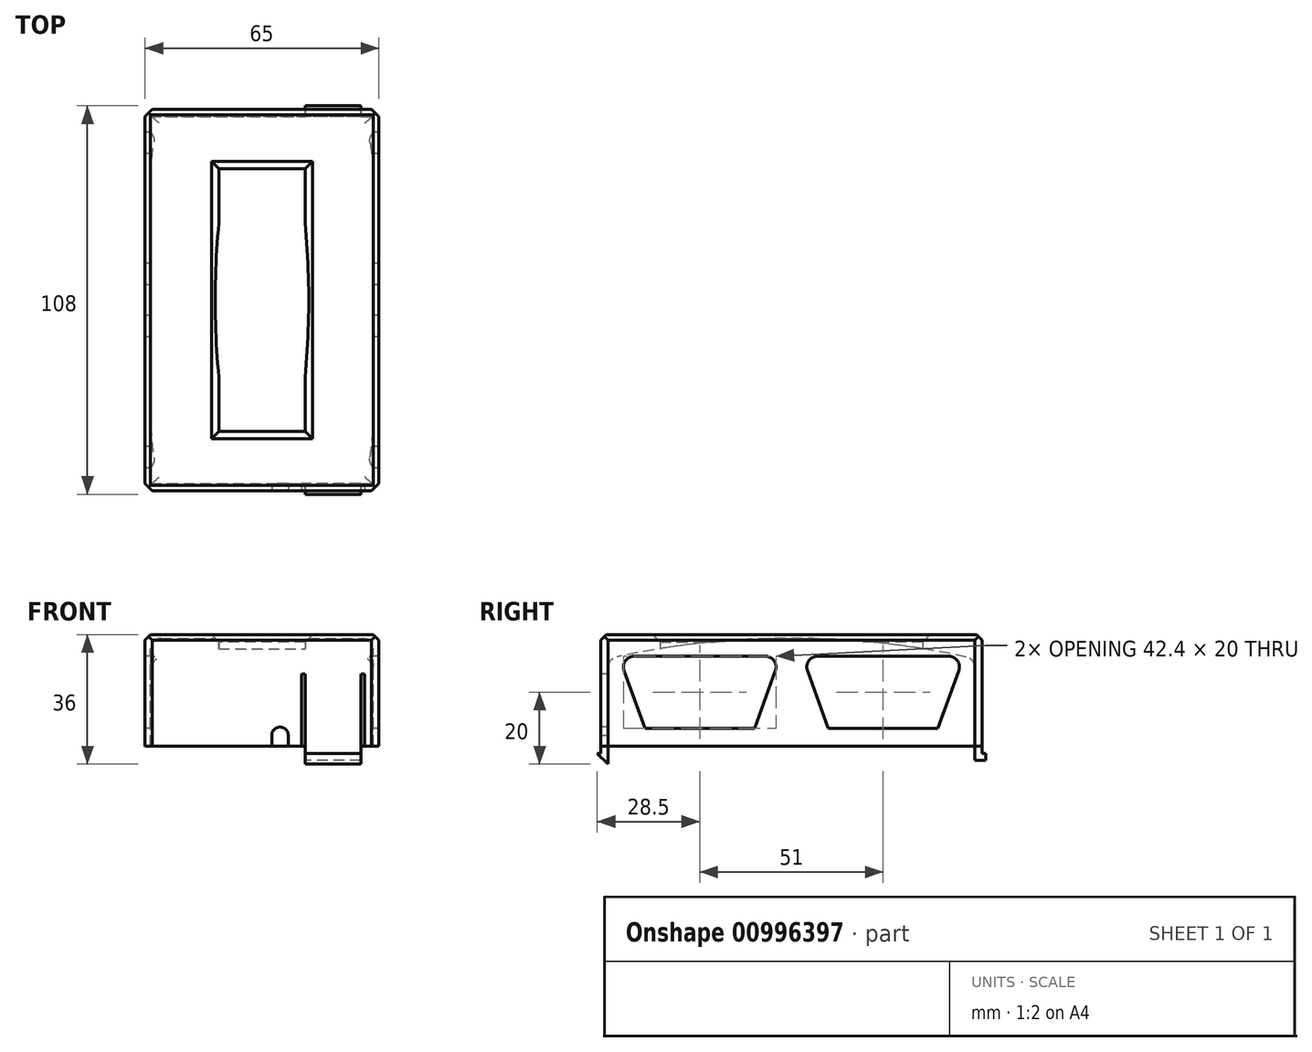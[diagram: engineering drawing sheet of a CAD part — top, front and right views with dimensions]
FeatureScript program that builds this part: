
annotation { "Feature Type Name" : "Feature", "Feature Type Description" : "" }
export const myFeature = defineFeature(function(context is Context, id is Id, definition is map)
    precondition{}
    {
        {
            var Q0;
            Q0=qCreatedBy(makeId("Top.planeOp"),FACE);
            var sketch = newSketch(context, id + "F0", { "sketchPlane" : qUnion([Q0])});
            skLineSegment(sketch, "E0.bottom", {"start": v(-32.5, 53) * mm, "end": v(32.5, 53) * mm});
            skLineSegment(sketch, "E0.top", {"start": v(-32.5, -53) * mm, "end": v(32.5, -53) * mm});
            skLineSegment(sketch, "E0.left", {"start": v(-32.5, 53) * mm, "end": v(-32.5, -53) * mm});
            skLineSegment(sketch, "E0.right", {"start": v(32.5, 53) * mm, "end": v(32.5, -53) * mm});
            skSolve(sketch);
        }
        {
            var Q0;
            Q0 = qSketchRegion(id + "F0", true);
            extrude(context, id + "F1", {"entities" : qUnion([Q0]), "depth" : 31 * mm, "offsetDistance" : 25 * mm});
        }
        {
            var Q0;
            Q0=qCreatedBy(makeId("Right.planeOp"),FACE);
            var sketch = newSketch(context, id + "F2", { "sketchPlane" : qUnion([Q0])});
            skLineSegment(sketch, "E1.bottom", {"start": v(-51, 0) * mm, "end": v(51, 0) * mm});
            skLineSegment(sketch, "E1.left", {"start": v(-51, 0) * mm, "end": v(-51, 24.27) * mm});
            skLineSegment(sketch, "E1.right", {"start": v(51, 0) * mm, "end": v(51, 24.27) * mm});
            skArc(sketch, "E2", {"start": v(51, 24.27) * mm, "mid": v(0, 30) * mm, "end": v(-51, 24.27) * mm});
            skSolve(sketch);
        }
        {
            var Q0;
            Q0 = qSketchRegion(id + "F2", true);
            extrude(context, id + "F3", {"entities" : qUnion([Q0]), "operationType" : NewBodyOperationType.REMOVE, "endBound" : BoundingType.SYMMETRIC, "oppositeDirection" : true, "depth" : 62 * mm, "offsetDistance" : 25 * mm});
        }
        {
            var Q0;
            Q0=qCreatedBy(makeId("Top.planeOp"),FACE);
            var sketch = newSketch(context, id + "F4", { "sketchPlane" : qUnion([Q0])});
            skLineSegment(sketch, "E3.bottom", {"start": v(-12, 36.5) * mm, "end": v(12, 36.5) * mm});
            skLineSegment(sketch, "E3.top", {"start": v(-12, -36.5) * mm, "end": v(12, -36.5) * mm});
            skLineSegment(sketch, "E3.left", {"start": v(-12, 36.5) * mm, "end": v(-12, -36.5) * mm});
            skLineSegment(sketch, "E3.right", {"start": v(12, 36.5) * mm, "end": v(12, -36.5) * mm});
            skSolve(sketch);
        }
        {
            var Q0;
            Q0 = qSketchRegion(id + "F4", true);
            extrude(context, id + "F5", {"entities" : qUnion([Q0]), "operationType" : NewBodyOperationType.REMOVE, "depth" : 58 * mm, "offsetDistance" : 25 * mm});
        }
        {
            var Q0;
            Q0=makeQuery(id+"F1.opExtrude","CAP_EDGE",EDGE,{"disambiguationData":[OSD([sQuery(id+"F0.wireOp",EDGE,"E0.bottom")])],"isStart":false});
            var Q1;
            Q1=makeQuery(id+"F1.opExtrude","CAP_EDGE",EDGE,{"disambiguationData":[OSD([sQuery(id+"F0.wireOp",EDGE,"E0.left")])],"isStart":false});
            var Q2;
            Q2=makeQuery(id+"F1.opExtrude","CAP_EDGE",EDGE,{"disambiguationData":[OSD([sQuery(id+"F0.wireOp",EDGE,"E0.right")])],"isStart":false});
            var Q3;
            Q3=makeQuery(id+"F1.opExtrude","CAP_EDGE",EDGE,{"disambiguationData":[OSD([sQuery(id+"F0.wireOp",EDGE,"E0.top")])],"isStart":false});
            chamfer(context, id + "F6", {"entities" : qUnion([Q0, Q1, Q2, Q3]), "width" : 1.5 * mm, "tangentPropagation" : true});
        }
        {
            var Q0;
            Q0=makeQuery(id+"F5.boolean.opBoolean","INTERSECT",EDGE,{"derivedFrom":[makeQuery(id+"F1.opExtrude","CAP_FACE",FACE,{"disambiguationData":[OSD([sQuery(id+"F0.wireOp",EDGE,"E0.bottom"),sQuery(id+"F0.wireOp",EDGE,"E0.top"),sQuery(id+"F0.wireOp",EDGE,"E0.left"),sQuery(id+"F0.wireOp",EDGE,"E0.right")])],"isStart":false}),makeQuery(id+"F5.opExtrude","SWEPT_FACE",FACE,{"disambiguationData":[OSD([sQuery(id+"F4.wireOp",EDGE,"E3.bottom")])]})]});
            var Q1;
            Q1=makeQuery(id+"F5.boolean.opBoolean","INTERSECT",EDGE,{"derivedFrom":[makeQuery(id+"F1.opExtrude","CAP_FACE",FACE,{"disambiguationData":[OSD([sQuery(id+"F0.wireOp",EDGE,"E0.bottom"),sQuery(id+"F0.wireOp",EDGE,"E0.top"),sQuery(id+"F0.wireOp",EDGE,"E0.left"),sQuery(id+"F0.wireOp",EDGE,"E0.right")])],"isStart":false}),makeQuery(id+"F5.opExtrude","SWEPT_FACE",FACE,{"disambiguationData":[OSD([sQuery(id+"F4.wireOp",EDGE,"E3.right")])]})]});
            var Q2;
            Q2=makeQuery(id+"F5.boolean.opBoolean","INTERSECT",EDGE,{"derivedFrom":[makeQuery(id+"F1.opExtrude","CAP_FACE",FACE,{"disambiguationData":[OSD([sQuery(id+"F0.wireOp",EDGE,"E0.bottom"),sQuery(id+"F0.wireOp",EDGE,"E0.top"),sQuery(id+"F0.wireOp",EDGE,"E0.left"),sQuery(id+"F0.wireOp",EDGE,"E0.right")])],"isStart":false}),makeQuery(id+"F5.opExtrude","SWEPT_FACE",FACE,{"disambiguationData":[OSD([sQuery(id+"F4.wireOp",EDGE,"E3.left")])]})]});
            var Q3;
            Q3=makeQuery(id+"F5.boolean.opBoolean","INTERSECT",EDGE,{"derivedFrom":[makeQuery(id+"F1.opExtrude","CAP_FACE",FACE,{"disambiguationData":[OSD([sQuery(id+"F0.wireOp",EDGE,"E0.bottom"),sQuery(id+"F0.wireOp",EDGE,"E0.top"),sQuery(id+"F0.wireOp",EDGE,"E0.left"),sQuery(id+"F0.wireOp",EDGE,"E0.right")])],"isStart":false}),makeQuery(id+"F5.opExtrude","SWEPT_FACE",FACE,{"disambiguationData":[OSD([sQuery(id+"F4.wireOp",EDGE,"E3.top")])]})]});
            chamfer(context, id + "F7", {"entities" : qUnion([Q0, Q1, Q2, Q3]), "width" : 2 * mm, "tangentPropagation" : true});
        }
        {
            var Q0;
            Q0=makeQuery(id+"F1.opExtrude","SWEPT_EDGE",EDGE,{"disambiguationData":[OSD([sQuery(id+"F0.wireOp",EDGE,"E0.bottom"),sQuery(id+"F0.wireOp",EDGE,"E0.left")])]});
            var Q1;
            Q1=makeQuery(id+"F1.opExtrude","SWEPT_EDGE",EDGE,{"disambiguationData":[OSD([sQuery(id+"F0.wireOp",EDGE,"E0.top"),sQuery(id+"F0.wireOp",EDGE,"E0.left")])]});
            var Q2;
            Q2=makeQuery(id+"F1.opExtrude","SWEPT_EDGE",EDGE,{"disambiguationData":[OSD([sQuery(id+"F0.wireOp",EDGE,"E0.top"),sQuery(id+"F0.wireOp",EDGE,"E0.right")])]});
            var Q3;
            Q3=makeQuery(id+"F1.opExtrude","SWEPT_EDGE",EDGE,{"disambiguationData":[OSD([sQuery(id+"F0.wireOp",EDGE,"E0.bottom"),sQuery(id+"F0.wireOp",EDGE,"E0.right")])]});
            chamfer(context, id + "F8", {"entities" : qUnion([Q0, Q1, Q2, Q3]), "width" : 2 * mm, "tangentPropagation" : true});
        }
        {
            var Q0;
            Q0=qCreatedBy(makeId("Right.planeOp"),FACE);
            var sketch = newSketch(context, id + "F9", { "sketchPlane" : qUnion([Q0])});
            skLineSegment(sketch, "E4", {"start": v(51, 0) * mm, "end": v(51, -4) * mm});
            skLineSegment(sketch, "E5", {"start": v(51, -4) * mm, "end": v(54, -4) * mm});
            skLineSegment(sketch, "E6", {"start": v(54, -4) * mm, "end": v(54, -2) * mm});
            skLineSegment(sketch, "E7", {"start": v(54, -2) * mm, "end": v(53, -2) * mm});
            skLineSegment(sketch, "E8", {"start": v(53, -2) * mm, "end": v(53, 0) * mm});
            skLineSegment(sketch, "E9", {"start": v(53, 0) * mm, "end": v(51, 0) * mm});
            skLineSegment(sketch, "E10", {"start": v(-51, 0) * mm, "end": v(-53, 0) * mm});
            skLineSegment(sketch, "E11", {"start": v(-53, 0) * mm, "end": v(-53, -2) * mm});
            skLineSegment(sketch, "E12", {"start": v(-53, -2) * mm, "end": v(-54, -2) * mm});
            skLineSegment(sketch, "E13", {"start": v(-54, -2) * mm, "end": v(-51, -5) * mm});
            skLineSegment(sketch, "E14", {"start": v(-51, -5) * mm, "end": v(-51, 0) * mm});
            skSolve(sketch);
        }
        {
            var Q0;
            Q0 = qSketchRegion(id + "F9", true);
            extrude(context, id + "F10", {"entities" : qUnion([Q0]), "operationType" : NewBodyOperationType.ADD, "depth" : 27.5 * mm, "offsetDistance" : 25 * mm, "hasSecondDirection" : true, "secondDirectionOppositeDirection" : false, "secondDirectionDepth" : 12 * mm});
        }
        {
            var Q0;
            Q0=makeQuery(id+"F10.boolean.opBoolean","MERGE",FACE,{"derivedFrom":[makeQuery(id+"F1.opExtrude","SWEPT_FACE",FACE,{"disambiguationData":[OSD([sQuery(id+"F0.wireOp",EDGE,"E0.top")])]}),makeQuery(id+"F10.opExtrude","SWEPT_FACE",FACE,{"disambiguationData":[OSD([sQuery(id+"F9.wireOp",EDGE,"E11")])]})]});
            var sketch = newSketch(context, id + "F11", { "sketchPlane" : qUnion([Q0])});
            skLineSegment(sketch, "E15.bottom", {"start": v(27.5, 0) * mm, "end": v(28.5, 0) * mm});
            skLineSegment(sketch, "E15.top", {"start": v(27.5, 20) * mm, "end": v(28.5, 20) * mm});
            skLineSegment(sketch, "E15.left", {"start": v(27.5, 0) * mm, "end": v(27.5, 20) * mm});
            skLineSegment(sketch, "E15.right", {"start": v(28.5, 0) * mm, "end": v(28.5, 20) * mm});
            skLineSegment(sketch, "E16.bottom", {"start": v(12, 0) * mm, "end": v(11, 0) * mm});
            skLineSegment(sketch, "E16.top", {"start": v(12, 20) * mm, "end": v(11, 20) * mm});
            skLineSegment(sketch, "E16.left", {"start": v(12, 0) * mm, "end": v(12, 20) * mm});
            skLineSegment(sketch, "E16.right", {"start": v(11, 0) * mm, "end": v(11, 20) * mm});
            skSolve(sketch);
        }
        {
            var Q0;
            Q0 = qSketchRegion(id + "F11", true);
            extrude(context, id + "F12", {"entities" : qUnion([Q0]), "operationType" : NewBodyOperationType.REMOVE, "oppositeDirection" : true, "depth" : 2 * mm, "offsetDistance" : 25 * mm});
        }
        {
            var Q0;
            Q0=makeQuery(id+"FG36ReWVNEU3biY_1.1.F10.boolean.opBoolean","MERGE",FACE,{"derivedFrom":[makeQuery(id+"F10.boolean.opBoolean","MERGE",FACE,{"derivedFrom":[makeQuery(id+"F1.opExtrude","SWEPT_FACE",FACE,{"disambiguationData":[OSD([sQuery(id+"F0.wireOp",EDGE,"E0.top")])]}),makeQuery(id+"F10.opExtrude","SWEPT_FACE",FACE,{"disambiguationData":[OSD([sQuery(id+"F9.wireOp",EDGE,"E11")])]})]}),makeQuery(id+"FG36ReWVNEU3biY_1.1.F10.opExtrude","SWEPT_FACE",FACE,{"disambiguationData":[OSD([sQuery(id+"FG36ReWVNEU3biY_1.1.F9.wireOp",EDGE,"E11")])]})]});
            var sketch = newSketch(context, id + "F13", { "sketchPlane" : qUnion([Q0])});
            skArc(sketch, "E17", {"start": v(7.3, 2.95) * mm, "mid": v(5, 5.3) * mm, "end": v(2.7, 2.94) * mm});
            skLineSegment(sketch, "E18", {"start": v(7.3, 2.95) * mm, "end": v(7.3, 0) * mm});
            skLineSegment(sketch, "E19", {"start": v(2.7, 2.94) * mm, "end": v(2.7, 0) * mm});
            skLineSegment(sketch, "E20", {"start": v(2.7, 0) * mm, "end": v(7.3, 0) * mm});
            skSolve(sketch);
        }
        {
            var Q0;
            Q0 = qSketchRegion(id + "F13", true);
            extrude(context, id + "F14", {"entities" : qUnion([Q0]), "operationType" : NewBodyOperationType.REMOVE, "oppositeDirection" : true, "depth" : 2 * mm, "offsetDistance" : 25 * mm});
        }
        {
            var Q0;
            Q0=makeQuery(id+"F3.boolean.opBoolean","COPY",EDGE,{"derivedFrom":makeQuery(id+"F3.opExtrude","SWEPT_EDGE",EDGE,{"disambiguationData":[OSD([sQuery(id+"F2.wireOp",EDGE,"E1.left"),sQuery(id+"F2.wireOp",EDGE,"E2")])]})});
            var Q1;
            Q1=makeQuery(id+"F3.boolean.opBoolean","COPY",EDGE,{"derivedFrom":makeQuery(id+"F3.opExtrude","CAP_EDGE",EDGE,{"disambiguationData":[OSD([sQuery(id+"F2.wireOp",EDGE,"E2")])],"isStart":false})});
            var Q2;
            Q2=makeQuery(id+"F3.boolean.opBoolean","COPY",EDGE,{"derivedFrom":makeQuery(id+"F3.opExtrude","CAP_EDGE",EDGE,{"disambiguationData":[OSD([sQuery(id+"F2.wireOp",EDGE,"E2")])],"isStart":true})});
            var Q3;
            Q3=makeQuery(id+"F3.boolean.opBoolean","COPY",EDGE,{"derivedFrom":makeQuery(id+"F3.opExtrude","SWEPT_EDGE",EDGE,{"disambiguationData":[OSD([sQuery(id+"F2.wireOp",EDGE,"E1.right"),sQuery(id+"F2.wireOp",EDGE,"E2")])]})});
            fillet(context, id + "F15", {"entities" : qUnion([Q0, Q1, Q2, Q3]), "radius" : 3 * mm, "tangentPropagation" : true, "allowEdgeOverflow" : false});
        }
        {
            var Q0;
            Q0=qCreatedBy(makeId("Right.planeOp"),FACE);
            var sketch = newSketch(context, id + "F16", { "sketchPlane" : qUnion([Q0])});
            skLineSegment(sketch, "E21", {"start": v(46.53, 20.97) * mm, "end": v(40.72, 5) * mm});
            skLineSegment(sketch, "E22", {"start": v(40.72, 5) * mm, "end": v(10.28, 5) * mm});
            skLineSegment(sketch, "E23", {"start": v(10.28, 5) * mm, "end": v(4.47, 20.97) * mm});
            skLineSegment(sketch, "E24", {"start": v(7.28, 25) * mm, "end": v(43.72, 25) * mm});
            skLineSegment(sketch, "E25.MirrorCS", {"start": v(-10.28, 5) * mm, "end": v(-4.47, 20.97) * mm});
            skLineSegment(sketch, "E26.MirrorCS", {"start": v(-7.28, 25) * mm, "end": v(-43.72, 25) * mm});
            skLineSegment(sketch, "E27.MirrorCS", {"start": v(-40.72, 5) * mm, "end": v(-10.28, 5) * mm});
            skLineSegment(sketch, "E28.MirrorCS", {"start": v(-46.53, 20.97) * mm, "end": v(-40.72, 5) * mm});
            skPoint(sketch, "E29.visualSharp", {"position": v(3, 25) * mm});
            skArc(sketch, "E29.filletArc", {"start": v(7.28, 25) * mm, "mid": v(4.83, 23.72) * mm, "end": v(4.47, 20.97) * mm});
            skPoint(sketch, "E30.visualSharp", {"position": v(48, 25) * mm});
            skArc(sketch, "E30.filletArc", {"start": v(46.53, 20.97) * mm, "mid": v(46.17, 23.72) * mm, "end": v(43.72, 25) * mm});
            skPoint(sketch, "E31.visualSharp", {"position": v(-3, 25) * mm});
            skArc(sketch, "E31.filletArc", {"start": v(-4.47, 20.97) * mm, "mid": v(-4.83, 23.72) * mm, "end": v(-7.28, 25) * mm});
            skPoint(sketch, "E32.visualSharp", {"position": v(-48, 25) * mm});
            skArc(sketch, "E32.filletArc", {"start": v(-43.72, 25) * mm, "mid": v(-46.17, 23.72) * mm, "end": v(-46.53, 20.97) * mm});
            skSolve(sketch);
        }
        {
            var Q0;
            Q0 = qSketchRegion(id + "F16", true);
            extrude(context, id + "F17", {"entities" : qUnion([Q0]), "operationType" : NewBodyOperationType.REMOVE, "endBound" : BoundingType.SYMMETRIC, "depth" : 65 * mm, "offsetDistance" : 25 * mm});
        }
    });
